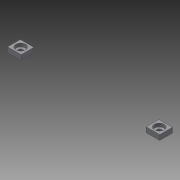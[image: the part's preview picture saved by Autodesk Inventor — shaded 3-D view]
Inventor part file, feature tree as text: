
AUTODESK INVENTOR PART (.ipt)
format: ipt  version: 2015 (Build 190159000, 159)  size: 153,600 bytes
history: native  units: mm
features: extrude x7, sketch x7, other x1, fillet x1
ambient origin geometry x8: Origin, YZ Plane, XZ Plane, XY Plane, X Axis, Y Axis, Z Axis, Center Point
bodies: Body1 (feature_tree), Body2 (feature_tree)
feature tree (16):
  other  "ソリッド1"
  extrude  "押し出し1"  Depth=90.0mm
  extrude  "押し出し2"  Depth=7.0mm
  extrude  "押し出し3"  Depth=3.0mm TaperAngle=0.0deg
  extrude  "押し出し4"  Depth=5.8mm
  fillet  "フィレット1"  Radius=5.8mm
  extrude  "押し出し5"  Depth=3.9mm
  extrude  "押し出し6"  Depth=3.9mm
  extrude  "押し出し7"  Depth=82.0mm
  sketch  "スケッチ1"
  sketch  "スケッチ2"
  sketch  "スケッチ3"
  sketch  "スケッチ4"
  sketch  "スケッチ6"
  sketch  "スケッチ7"
  sketch  "スケッチ8"
